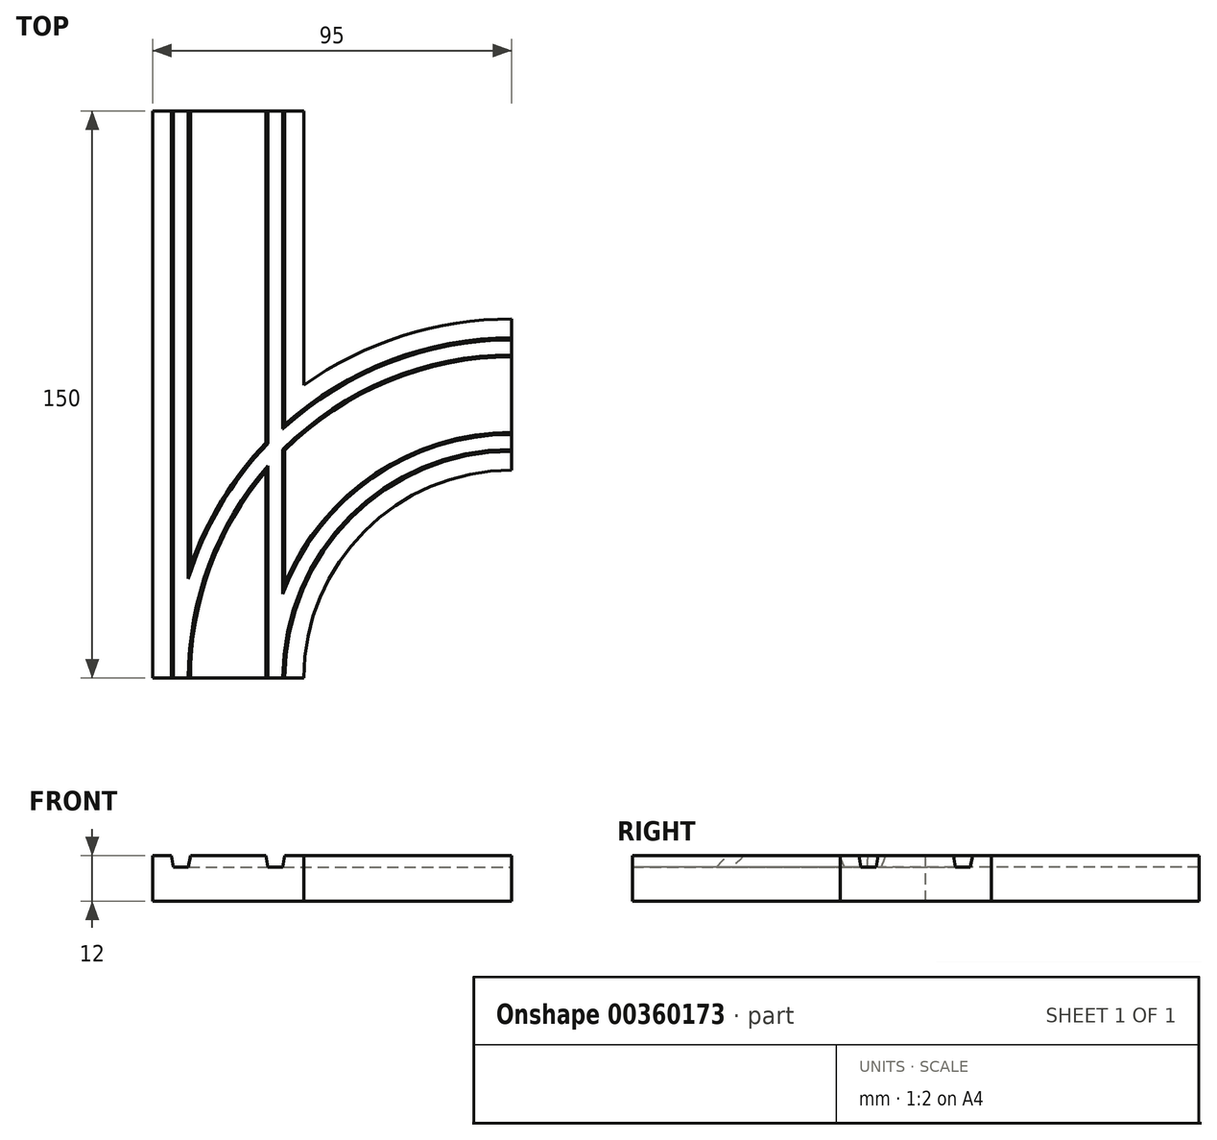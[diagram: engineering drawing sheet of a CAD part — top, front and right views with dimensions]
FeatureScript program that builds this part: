
annotation { "Feature Type Name" : "Feature", "Feature Type Description" : "" }
export const myFeature = defineFeature(function(context is Context, id is Id, definition is map)
    precondition{}
    {
        {
            var Q0;
            Q0=qCreatedBy(makeId("Front.planeOp"),FACE);
            var sketch = newSketch(context, id + "F0", { "sketchPlane" : qUnion([Q0])});
            skLineSegment(sketch, "E0", {"start": v(-20, 2.74) * mm, "end": v(-20, -9.26) * mm});
            skLineSegment(sketch, "E1", {"start": v(-20, -9.26) * mm, "end": v(20, -9.26) * mm});
            skLineSegment(sketch, "E2", {"start": v(20, -9.26) * mm, "end": v(20, 2.74) * mm});
            skLineSegment(sketch, "E3", {"start": v(-10, 2.74) * mm, "end": v(-10.53, -0.26) * mm});
            skLineSegment(sketch, "E4", {"start": v(-10.53, -0.26) * mm, "end": v(-14.47, -0.26) * mm});
            skLineSegment(sketch, "E5", {"start": v(-14.47, -0.26) * mm, "end": v(-15, 2.74) * mm});
            skLineSegment(sketch, "E6", {"start": v(-15, 2.74) * mm, "end": v(-20, 2.74) * mm});
            skLineSegment(sketch, "E7", {"start": v(-12.5, 6.87) * mm, "end": v(-12.5, -3.7) * mm, "construction": true});
            skLineSegment(sketch, "E8.MirrorCS", {"start": v(10, 2.74) * mm, "end": v(10.53, -0.26) * mm});
            skLineSegment(sketch, "E9.MirrorCS", {"start": v(15, 2.74) * mm, "end": v(20, 2.74) * mm});
            skLineSegment(sketch, "E10.MirrorCS", {"start": v(14.47, -0.26) * mm, "end": v(15, 2.74) * mm});
            skLineSegment(sketch, "E11.MirrorCS", {"start": v(12.5, 6.87) * mm, "end": v(12.5, -3.7) * mm, "construction": true});
            skLineSegment(sketch, "E12.MirrorCS", {"start": v(10.53, -0.26) * mm, "end": v(14.47, -0.26) * mm});
            skLineSegment(sketch, "E13", {"start": v(-10, 2.74) * mm, "end": v(10, 2.74) * mm});
            skSolve(sketch);
        }
        {
            var Q0;
            Q0 = qSketchRegion(id + "F0", true);
            var Q1;
            Q1=sQuery(id+"F0.wireOp",EDGE,"E0");
            var Q2;
            Q2=sQuery(id+"F0.wireOp",EDGE,"E1");
            var Q3;
            Q3=sQuery(id+"F0.wireOp",EDGE,"E2");
            var Q4;
            Q4=sQuery(id+"F0.wireOp",EDGE,"E3");
            var Q5;
            Q5=sQuery(id+"F0.wireOp",EDGE,"E4");
            var Q6;
            Q6=sQuery(id+"F0.wireOp",EDGE,"E5");
            var Q7;
            Q7=sQuery(id+"F0.wireOp",EDGE,"E6");
            var Q8;
            Q8=sQuery(id+"F0.wireOp",EDGE,"E8.MirrorCS");
            var Q9;
            Q9=sQuery(id+"F0.wireOp",EDGE,"E9.MirrorCS");
            var Q10;
            Q10=sQuery(id+"F0.wireOp",EDGE,"E10.MirrorCS");
            var Q11;
            Q11=sQuery(id+"F0.wireOp",EDGE,"E12.MirrorCS");
            var Q12;
            Q12=sQuery(id+"F0.wireOp",EDGE,"E13");
            extrude(context, id + "F1", {"entities" : qUnion([Q0]), "surfaceEntities" : qUnion([Q1, Q2, Q3, Q4, Q5, Q6, Q7, Q8, Q9, Q10, Q11, Q12]), "oppositeDirection" : true, "depth" : 150 * mm});
        }
        {
            var Q0;
            Q0=qCreatedBy(makeId("Top.planeOp"),FACE);
            var sketch = newSketch(context, id + "F2", { "sketchPlane" : qUnion([Q0])});
            skLineSegment(sketch, "E14", {"start": v(-75, 0) * mm, "end": v(75, 0) * mm, "construction": true});
            skLineSegment(sketch, "E15", {"start": v(75, 0) * mm, "end": v(75, 150) * mm, "construction": true});
            skLineSegment(sketch, "E16", {"start": v(75, 150) * mm, "end": v(-75, 150) * mm, "construction": true});
            skLineSegment(sketch, "E17", {"start": v(-75, 150) * mm, "end": v(-75, 0) * mm, "construction": true});
            skPoint(sketch, "E18", {"position": v(75, 75) * mm});
            skArc(sketch, "E19", {"start": v(75, 75) * mm, "mid": v(21.97, 53.03) * mm, "end": v(0, 0) * mm});
            skSolve(sketch);
        }
        {
            var Q0;
            Q0 = qSketchRegion(id + "F0", true);
            var Q1;
            Q1 = qConstructionFilter(qBodyType(qCreatedBy(id + "F2" ,EDGE), BodyType.WIRE), ConstructionObject.NO);
            sweep(context, id + "F3", {"operationType" : NewBodyOperationType.ADD, "profiles" : qUnion([Q0]), "path" : qUnion([Q1])});
        }
        {
            var Q0;
            Q0=makeQuery(id+"F1.opExtrude","CAP_FACE",FACE,{"disambiguationData":[OSD([sQuery(id+"F0.wireOp",EDGE,"E0"),sQuery(id+"F0.wireOp",EDGE,"E1"),sQuery(id+"F0.wireOp",EDGE,"E2"),sQuery(id+"F0.wireOp",EDGE,"E3"),sQuery(id+"F0.wireOp",EDGE,"E4"),sQuery(id+"F0.wireOp",EDGE,"E5"),sQuery(id+"F0.wireOp",EDGE,"E6"),sQuery(id+"F0.wireOp",EDGE,"E8.MirrorCS"),sQuery(id+"F0.wireOp",EDGE,"E9.MirrorCS"),sQuery(id+"F0.wireOp",EDGE,"E10.MirrorCS"),sQuery(id+"F0.wireOp",EDGE,"E12.MirrorCS"),sQuery(id+"F0.wireOp",EDGE,"E13")])],"isStart":true});
            var sketch = newSketch(context, id + "F4", { "sketchPlane" : qUnion([Q0])});
            skLineSegment(sketch, "E20", {"start": v(-15, 2.74) * mm, "end": v(-14.47, -0.26) * mm});
            skLineSegment(sketch, "E21", {"start": v(-14.47, -0.26) * mm, "end": v(-10.53, -0.26) * mm});
            skLineSegment(sketch, "E22", {"start": v(-10.53, -0.26) * mm, "end": v(-10, 2.74) * mm});
            skLineSegment(sketch, "E23", {"start": v(-10, 2.74) * mm, "end": v(-15, 2.74) * mm});
            skLineSegment(sketch, "E24", {"start": v(10, 2.74) * mm, "end": v(10.53, -0.26) * mm});
            skLineSegment(sketch, "E25", {"start": v(10.53, -0.26) * mm, "end": v(14.47, -0.26) * mm});
            skLineSegment(sketch, "E26", {"start": v(14.47, -0.26) * mm, "end": v(15, 2.74) * mm});
            skLineSegment(sketch, "E27", {"start": v(15, 2.74) * mm, "end": v(10, 2.74) * mm});
            skSolve(sketch);
        }
        {
            var Q0;
            Q0 = qSketchRegion(id + "F4", true);
            var Q1;
            Q1=makeQuery(id+"F1.opExtrude","CAP_FACE",FACE,{"disambiguationData":[OSD([sQuery(id+"F0.wireOp",EDGE,"E0"),sQuery(id+"F0.wireOp",EDGE,"E1"),sQuery(id+"F0.wireOp",EDGE,"E2"),sQuery(id+"F0.wireOp",EDGE,"E3"),sQuery(id+"F0.wireOp",EDGE,"E4"),sQuery(id+"F0.wireOp",EDGE,"E5"),sQuery(id+"F0.wireOp",EDGE,"E6"),sQuery(id+"F0.wireOp",EDGE,"E8.MirrorCS"),sQuery(id+"F0.wireOp",EDGE,"E9.MirrorCS"),sQuery(id+"F0.wireOp",EDGE,"E10.MirrorCS"),sQuery(id+"F0.wireOp",EDGE,"E12.MirrorCS"),sQuery(id+"F0.wireOp",EDGE,"E13")])],"isStart":false});
            extrude(context, id + "F5", {"entities" : qUnion([Q0]), "operationType" : NewBodyOperationType.REMOVE, "endBound" : BoundingType.UP_TO_SURFACE, "oppositeDirection" : true, "endBoundEntityFace" : qUnion([Q1]), "depth" : 25 * mm});
        }
        {
            var Q0;
            Q0 = qSketchRegion(id + "F4", true);
            var Q1;
            Q1 = qConstructionFilter(qBodyType(qCreatedBy(id + "F2" ,EDGE), BodyType.WIRE), ConstructionObject.NO);
            sweep(context, id + "F6", {"operationType" : NewBodyOperationType.REMOVE, "profiles" : qUnion([Q0]), "path" : qUnion([Q1])});
        }
    });
